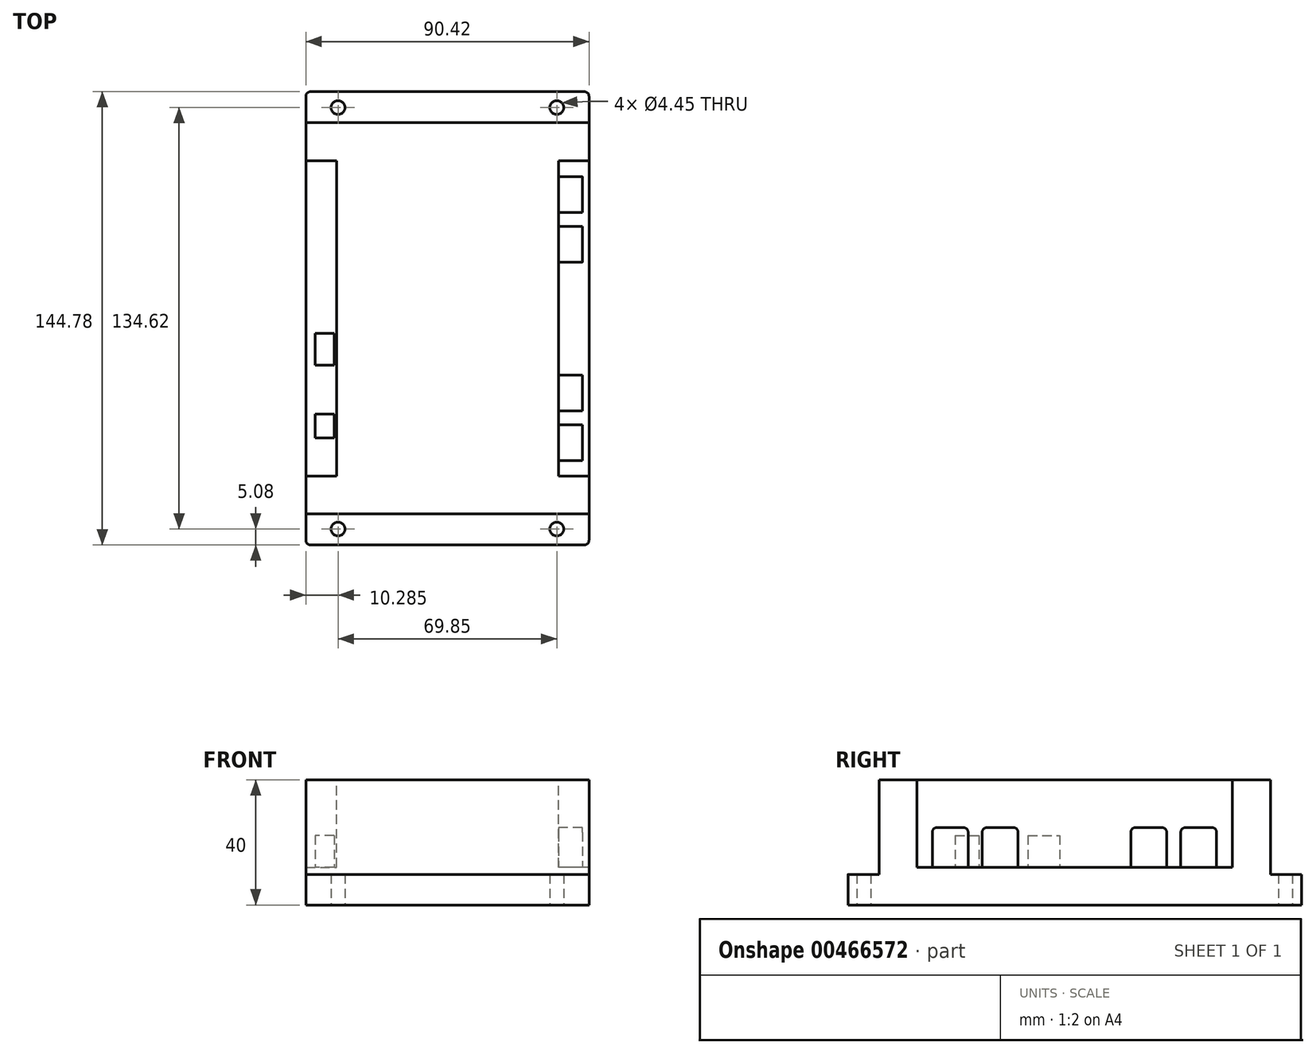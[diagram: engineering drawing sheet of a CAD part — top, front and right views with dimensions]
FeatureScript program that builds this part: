
annotation { "Feature Type Name" : "Feature", "Feature Type Description" : "" }
export const myFeature = defineFeature(function(context is Context, id is Id, definition is map)
    precondition{}
    {
        {
            var Q0;
            Q0=qCreatedBy(makeId("Top.planeOp"),FACE);
            var sketch = newSketch(context, id + "F0", { "sketchPlane" : qUnion([Q0])});
            skLineSegment(sketch, "E0.bottom", {"start": v(-45.21, 72.4) * mm, "end": v(45.21, 72.4) * mm});
            skLineSegment(sketch, "E0.top", {"start": v(-45.21, -72.4) * mm, "end": v(45.21, -72.4) * mm});
            skLineSegment(sketch, "E0.left", {"start": v(-45.21, 72.4) * mm, "end": v(-45.21, -72.4) * mm});
            skLineSegment(sketch, "E0.right", {"start": v(45.21, 72.4) * mm, "end": v(45.21, -72.4) * mm});
            skPoint(sketch, "E0.middle", {"position": v(0, 0) * mm});
            skSolve(sketch);
        }
        {
            var Q0;
            Q0 = qSketchRegion(id + "F0", true);
            extrude(context, id + "F1", {"entities" : qUnion([Q0]), "depth" : 40 * mm});
        }
        {
            var Q0;
            Q0=makeQuery(id+"F1.opExtrude","CAP_FACE",FACE,{"disambiguationData":[OSD([sQuery(id+"F0.wireOp",EDGE,"E0.bottom"),sQuery(id+"F0.wireOp",EDGE,"E0.top"),sQuery(id+"F0.wireOp",EDGE,"E0.left"),sQuery(id+"F0.wireOp",EDGE,"E0.right")])],"isStart":false});
            var sketch = newSketch(context, id + "F2", { "sketchPlane" : qUnion([Q0])});
            skLineSegment(sketch, "E1.bottom", {"start": v(-78.54, -62.48) * mm, "end": v(76.72, -62.48) * mm});
            skLineSegment(sketch, "E1.top", {"start": v(-78.54, -102.44) * mm, "end": v(76.72, -102.44) * mm});
            skLineSegment(sketch, "E1.left", {"start": v(-78.54, -102.44) * mm, "end": v(-78.54, -62.48) * mm});
            skLineSegment(sketch, "E1.right", {"start": v(76.72, -102.44) * mm, "end": v(76.72, -62.48) * mm});
            skLineSegment(sketch, "E2.bottom", {"start": v(-69.98, 80.03) * mm, "end": v(68.82, 80.03) * mm});
            skLineSegment(sketch, "E2.top", {"start": v(-69.98, 62.48) * mm, "end": v(68.82, 62.48) * mm});
            skLineSegment(sketch, "E2.left", {"start": v(-69.98, 80.03) * mm, "end": v(-69.98, 62.48) * mm});
            skLineSegment(sketch, "E2.right", {"start": v(68.82, 80.03) * mm, "end": v(68.82, 62.48) * mm});
            skSolve(sketch);
        }
        {
            var Q0;
            Q0 = qSketchRegion(id + "F2", true);
            extrude(context, id + "F3", {"entities" : qUnion([Q0]), "operationType" : NewBodyOperationType.REMOVE, "oppositeDirection" : true, "depth" : 30.23 * mm});
        }
        {
            var Q0;
            Q0=makeQuery(id+"F1.opExtrude","SWEPT_EDGE",EDGE,{"disambiguationData":[OSD([sQuery(id+"F0.wireOp",EDGE,"E0.top"),sQuery(id+"F0.wireOp",EDGE,"E0.right")])]});
            var Q1;
            Q1=makeQuery(id+"F1.opExtrude","SWEPT_EDGE",EDGE,{"disambiguationData":[OSD([sQuery(id+"F0.wireOp",EDGE,"E0.top"),sQuery(id+"F0.wireOp",EDGE,"E0.left")])]});
            var Q2;
            Q2=makeQuery(id+"F1.opExtrude","SWEPT_EDGE",EDGE,{"disambiguationData":[OSD([sQuery(id+"F0.wireOp",EDGE,"E0.bottom"),sQuery(id+"F0.wireOp",EDGE,"E0.right")])]});
            var Q3;
            Q3=makeQuery(id+"F1.opExtrude","SWEPT_EDGE",EDGE,{"disambiguationData":[OSD([sQuery(id+"F0.wireOp",EDGE,"E0.bottom"),sQuery(id+"F0.wireOp",EDGE,"E0.left")])]});
            fillet(context, id + "F4", {"entities" : qUnion([Q0, Q1, Q2, Q3]), "radius" : 1.52 * mm, "tangentPropagation" : true, "allowEdgeOverflow" : false});
        }
        {
            var Q0;
            Q0=makeQuery(id+"F1.opExtrude","CAP_FACE",FACE,{"disambiguationData":[OSD([sQuery(id+"F0.wireOp",EDGE,"E0.bottom"),sQuery(id+"F0.wireOp",EDGE,"E0.top"),sQuery(id+"F0.wireOp",EDGE,"E0.left"),sQuery(id+"F0.wireOp",EDGE,"E0.right")])],"isStart":true});
            var sketch = newSketch(context, id + "F5", { "sketchPlane" : qUnion([Q0])});
            skLineSegment(sketch, "E3.bottom", {"start": v(34.92, 67.31) * mm, "end": v(-34.93, 67.31) * mm, "construction": true});
            skLineSegment(sketch, "E3.top", {"start": v(34.92, -67.31) * mm, "end": v(-34.93, -67.31) * mm, "construction": true});
            skLineSegment(sketch, "E3.left", {"start": v(34.92, 67.31) * mm, "end": v(34.92, -67.31) * mm, "construction": true});
            skLineSegment(sketch, "E3.right", {"start": v(-34.93, 67.31) * mm, "end": v(-34.93, -67.31) * mm, "construction": true});
            skPoint(sketch, "E3.middle", {"position": v(0, 0) * mm});
            skCircle(sketch, "E4", {"center": v(-34.93, 67.31) * mm, "radius": 2.22 * mm});
            skCircle(sketch, "E5", {"center": v(34.92, 67.31) * mm, "radius": 2.22 * mm});
            skCircle(sketch, "E6", {"center": v(34.92, -67.31) * mm, "radius": 2.22 * mm});
            skCircle(sketch, "E7", {"center": v(-34.93, -67.31) * mm, "radius": 2.22 * mm});
            skSolve(sketch);
        }
        {
            var Q0;
            Q0 = qSketchRegion(id + "F5", true);
            extrude(context, id + "F6", {"entities" : qUnion([Q0]), "operationType" : NewBodyOperationType.REMOVE, "oppositeDirection" : true, "depth" : 25.4 * mm});
        }
        {
            var Q0;
            Q0=makeQuery(id+"F1.opExtrude","CAP_FACE",FACE,{"disambiguationData":[OSD([sQuery(id+"F0.wireOp",EDGE,"E0.bottom"),sQuery(id+"F0.wireOp",EDGE,"E0.top"),sQuery(id+"F0.wireOp",EDGE,"E0.left"),sQuery(id+"F0.wireOp",EDGE,"E0.right")])],"isStart":false});
            var sketch = newSketch(context, id + "F7", { "sketchPlane" : qUnion([Q0])});
            skLineSegment(sketch, "E8.bottom", {"start": v(-61.26, -50.36) * mm, "end": v(-35.43, -50.36) * mm});
            skLineSegment(sketch, "E8.top", {"start": v(-61.26, 50.36) * mm, "end": v(-35.43, 50.36) * mm});
            skLineSegment(sketch, "E8.left", {"start": v(-61.26, -50.36) * mm, "end": v(-61.26, 50.36) * mm});
            skLineSegment(sketch, "E8.right", {"start": v(-35.43, -50.36) * mm, "end": v(-35.43, 50.36) * mm});
            skLineSegment(sketch, "E9.bottom", {"start": v(61.26, -50.36) * mm, "end": v(35.43, -50.36) * mm});
            skLineSegment(sketch, "E9.top", {"start": v(61.26, 50.36) * mm, "end": v(35.43, 50.36) * mm});
            skLineSegment(sketch, "E9.left", {"start": v(61.26, -50.36) * mm, "end": v(61.26, 50.36) * mm});
            skLineSegment(sketch, "E9.right", {"start": v(35.43, -50.36) * mm, "end": v(35.43, 50.36) * mm});
            skLineSegment(sketch, "E10", {"start": v(-35.43, 0) * mm, "end": v(0, 0) * mm, "construction": true});
            skSolve(sketch);
        }
        {
            var Q0;
            Q0 = qSketchRegion(id + "F7", true);
            extrude(context, id + "F8", {"entities" : qUnion([Q0]), "operationType" : NewBodyOperationType.REMOVE, "oppositeDirection" : true, "depth" : 27.94 * mm});
        }
        {
            var Q0;
            Q0=makeQuery(id+"F8.boolean.opBoolean","COPY",FACE,{"derivedFrom":makeQuery(id+"F8.opExtrude","CAP_FACE",FACE,{"disambiguationData":[OSD([sQuery(id+"F7.wireOp",EDGE,"E9.bottom"),sQuery(id+"F7.wireOp",EDGE,"E9.top"),sQuery(id+"F7.wireOp",EDGE,"E9.left"),sQuery(id+"F7.wireOp",EDGE,"E9.right")])],"isStart":false})});
            var sketch = newSketch(context, id + "F9", { "sketchPlane" : qUnion([Q0])});
            skLineSegment(sketch, "E11.bottom", {"start": v(43.05, 45.28) * mm, "end": v(35.43, 45.28) * mm});
            skLineSegment(sketch, "E11.top", {"start": v(43.05, 33.85) * mm, "end": v(35.43, 33.85) * mm});
            skLineSegment(sketch, "E11.left", {"start": v(43.05, 45.28) * mm, "end": v(43.05, 33.85) * mm});
            skLineSegment(sketch, "E11.right", {"start": v(35.43, 45.28) * mm, "end": v(35.43, 33.85) * mm});
            skLineSegment(sketch, "E12.bottom", {"start": v(43.05, 29.33) * mm, "end": v(35.43, 29.33) * mm});
            skLineSegment(sketch, "E12.top", {"start": v(43.05, 17.9) * mm, "end": v(35.43, 17.9) * mm});
            skLineSegment(sketch, "E12.left", {"start": v(43.05, 29.33) * mm, "end": v(43.05, 17.9) * mm});
            skLineSegment(sketch, "E12.right", {"start": v(35.43, 29.33) * mm, "end": v(35.43, 17.9) * mm});
            skLineSegment(sketch, "E13.bottom", {"start": v(43.05, -18.12) * mm, "end": v(35.43, -18.12) * mm});
            skLineSegment(sketch, "E13.top", {"start": v(43.05, -29.55) * mm, "end": v(35.43, -29.55) * mm});
            skLineSegment(sketch, "E13.left", {"start": v(43.05, -18.12) * mm, "end": v(43.05, -29.55) * mm});
            skLineSegment(sketch, "E13.right", {"start": v(35.43, -18.12) * mm, "end": v(35.43, -29.55) * mm});
            skLineSegment(sketch, "E14.bottom", {"start": v(43.05, -34.07) * mm, "end": v(35.43, -34.07) * mm});
            skLineSegment(sketch, "E14.top", {"start": v(43.05, -45.5) * mm, "end": v(35.43, -45.5) * mm});
            skLineSegment(sketch, "E14.left", {"start": v(43.05, -34.07) * mm, "end": v(43.05, -45.5) * mm});
            skLineSegment(sketch, "E14.right", {"start": v(35.43, -34.07) * mm, "end": v(35.43, -45.5) * mm});
            skSolve(sketch);
        }
        {
            var Q0;
            Q0 = qSketchRegion(id + "F9", true);
            extrude(context, id + "F10", {"entities" : qUnion([Q0]), "operationType" : NewBodyOperationType.ADD, "depth" : 12.7 * mm});
        }
        {
            var Q0;
            Q0=makeQuery(id+"F10.opExtrude","CAP_EDGE",EDGE,{"disambiguationData":[OSD([sQuery(id+"F9.wireOp",EDGE,"E14.top")])],"isStart":false});
            var Q1;
            Q1=makeQuery(id+"F10.opExtrude","CAP_EDGE",EDGE,{"disambiguationData":[OSD([sQuery(id+"F9.wireOp",EDGE,"E14.bottom")])],"isStart":false});
            var Q2;
            Q2=makeQuery(id+"F10.opExtrude","CAP_EDGE",EDGE,{"disambiguationData":[OSD([sQuery(id+"F9.wireOp",EDGE,"E13.top")])],"isStart":false});
            var Q3;
            Q3=makeQuery(id+"F10.opExtrude","CAP_EDGE",EDGE,{"disambiguationData":[OSD([sQuery(id+"F9.wireOp",EDGE,"E13.bottom")])],"isStart":false});
            var Q4;
            Q4=makeQuery(id+"F10.opExtrude","CAP_EDGE",EDGE,{"disambiguationData":[OSD([sQuery(id+"F9.wireOp",EDGE,"E12.top")])],"isStart":false});
            var Q5;
            Q5=makeQuery(id+"F10.opExtrude","CAP_EDGE",EDGE,{"disambiguationData":[OSD([sQuery(id+"F9.wireOp",EDGE,"E11.top")])],"isStart":false});
            var Q6;
            Q6=makeQuery(id+"F10.opExtrude","CAP_EDGE",EDGE,{"disambiguationData":[OSD([sQuery(id+"F9.wireOp",EDGE,"E12.bottom")])],"isStart":false});
            var Q7;
            Q7=makeQuery(id+"F10.opExtrude","CAP_EDGE",EDGE,{"disambiguationData":[OSD([sQuery(id+"F9.wireOp",EDGE,"E11.bottom")])],"isStart":false});
            fillet(context, id + "F11", {"entities" : qUnion([Q0, Q1, Q2, Q3, Q4, Q5, Q6, Q7]), "radius" : 1.52 * mm, "tangentPropagation" : true, "allowEdgeOverflow" : false});
        }
        {
            var Q0;
            Q0=makeQuery(id+"F8.boolean.opBoolean","COPY",FACE,{"derivedFrom":makeQuery(id+"F8.opExtrude","CAP_FACE",FACE,{"disambiguationData":[OSD([sQuery(id+"F7.wireOp",EDGE,"E8.bottom"),sQuery(id+"F7.wireOp",EDGE,"E8.top"),sQuery(id+"F7.wireOp",EDGE,"E8.left"),sQuery(id+"F7.wireOp",EDGE,"E8.right")])],"isStart":false})});
            var sketch = newSketch(context, id + "F12", { "sketchPlane" : qUnion([Q0])});
            skLineSegment(sketch, "E15.bottom", {"start": v(-36.2, -38.17) * mm, "end": v(-42.3, -38.17) * mm});
            skLineSegment(sketch, "E15.top", {"start": v(-36.2, -30.55) * mm, "end": v(-42.3, -30.55) * mm});
            skLineSegment(sketch, "E15.left", {"start": v(-36.2, -38.17) * mm, "end": v(-36.2, -30.55) * mm});
            skLineSegment(sketch, "E15.right", {"start": v(-42.3, -38.17) * mm, "end": v(-42.3, -30.55) * mm});
            skLineSegment(sketch, "E16.bottom", {"start": v(-36.2, -14.98) * mm, "end": v(-42.3, -14.98) * mm});
            skLineSegment(sketch, "E16.top", {"start": v(-36.2, -4.82) * mm, "end": v(-42.3, -4.82) * mm});
            skLineSegment(sketch, "E16.left", {"start": v(-36.2, -14.98) * mm, "end": v(-36.2, -4.82) * mm});
            skLineSegment(sketch, "E16.right", {"start": v(-42.3, -14.98) * mm, "end": v(-42.3, -4.82) * mm});
            skSolve(sketch);
        }
        {
            var Q0;
            Q0 = qSketchRegion(id + "F12", true);
            extrude(context, id + "F13", {"entities" : qUnion([Q0]), "operationType" : NewBodyOperationType.ADD, "depth" : 10.16 * mm});
        }
    });
